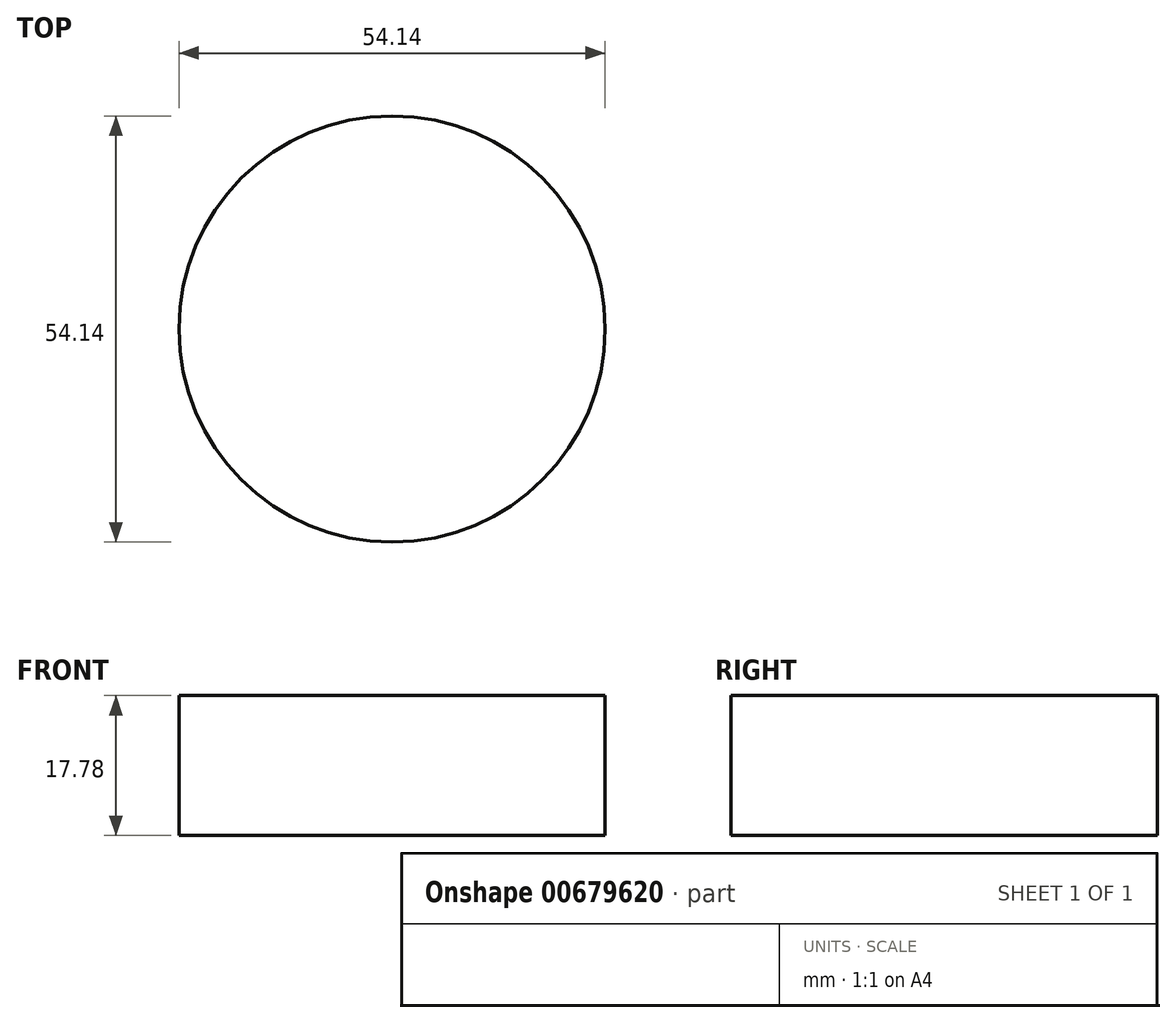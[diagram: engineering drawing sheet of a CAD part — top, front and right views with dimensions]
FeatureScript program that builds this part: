
annotation { "Feature Type Name" : "Feature", "Feature Type Description" : "" }
export const myFeature = defineFeature(function(context is Context, id is Id, definition is map)
    precondition{}
    {
        {
            var Q0;
            Q0=qCreatedBy(makeId("Top.planeOp"),FACE);
            var sketch = newSketch(context, id + "F0", { "sketchPlane" : qUnion([Q0])});
            skCircle(sketch, "E0", {"center": v(0, 0) * mm, "radius": 27.07 * mm});
            skSolve(sketch);
        }
        {
            var Q0;
            Q0=makeQuery(id+"F0.imprint","IMPRINT",FACE,{"disambiguationData":[TD([[makeQuery(id+"F0.imprint","IMPRINT",EDGE,{"derivedFrom":sQuery(id+"F0.wireOp",EDGE,"E0")}),1.0]])]});
            var sketch = newSketch(context, id + "F1", { "sketchPlane" : qUnion([Q0])});
            skSolve(sketch);
        }
        {
            var Q0;
            Q0=qCreatedBy(makeId("Top.planeOp"),FACE);
            var sketch = newSketch(context, id + "F2", { "sketchPlane" : qUnion([Q0])});
            skCircle(sketch, "E1", {"center": v(0, 0) * mm, "radius": 6.67 * mm});
            skSolve(sketch);
        }
        {
            var Q0;
            Q0=sQuery(id+"F2.wireOp",EDGE,"E1");
            extrude(context, id + "F3", {"bodyType" : ToolBodyType.SURFACE, "surfaceEntities" : qUnion([Q0]), "depth" : 12.7 * mm, "offsetDistance" : 25.4 * mm});
        }
        {
            var Q0;
            Q0=makeQuery(id+"F1.imprint","IMPRINT",FACE,{"disambiguationData":[TD([[makeQuery(id+"F1.imprint","IMPRINT",EDGE,{"derivedFrom":makeQuery(id+"F0.imprint","IMPRINT",EDGE,{"derivedFrom":sQuery(id+"F0.wireOp",EDGE,"E0")})}),1.0]])]});
            extrude(context, id + "F4", {"entities" : qUnion([Q0]), "oppositeDirection" : true, "depth" : 17.78 * mm, "offsetDistance" : 25.4 * mm});
        }
    });
